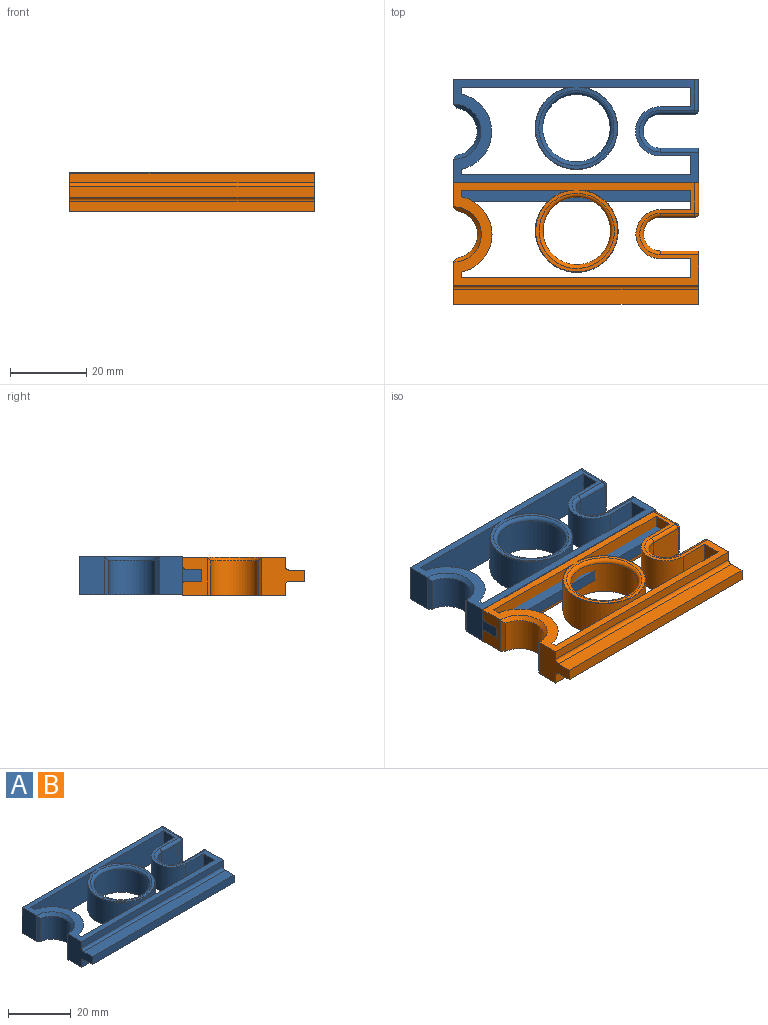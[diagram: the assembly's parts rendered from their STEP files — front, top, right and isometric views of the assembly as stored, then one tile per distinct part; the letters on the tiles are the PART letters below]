
ASSEMBLY  parts=2 mates=1
PART A: 48 faces, bbox 64.2x32x10.1 mm
  f0: plane 64.13x26.92mm, normal (0,0,1), area 447.9mm2, adj f1,f2,f3,f4,f5,f9,f17,f18
  f1: plane 10x8.96mm, normal (1,0,0), area 89.2mm2, adj f0,f5,f7,f13,f14,f17
  f2: plane 11.13x10mm, normal (-1,0,0), area 76.7mm2, adj f0,f5,f7,f21,f22,f36,f38,f39
  f3: plane 64.13x10mm, normal (0,1,0), area 640.9mm2, adj f0,f4,f6,f7,f43,f47
  f4: plane 10x6.46mm, normal (-1,0,0), area 64.6mm2, adj f0,f3,f7,f20,f21
  f5: plane 64.13x10mm, normal (0,-1,0), area 321.3mm2, adj f0,f1,f2,f7,f37,f40,f41
  f6: plane 8.1x8mm, normal (1,0,0), area 64.8mm2, adj f3,f43,f45,f47
  f7: plane 64.13x26.92mm, normal (0,0,-1), area 488.3mm2, adj f1,f2,f3,f4,f5,f8,f10,f14
  f8: cylinder r=8.83mm len=17.67mm, axis (0,0,1), area 499.5mm2, adj f7,f9
  f9: torus R=9.83mm, axis (0,0,1), area 90.8mm2, adj f0,f8
  f10: cylinder r=6.24mm len=12.35mm, axis (0,0,1), area 160.5mm2, adj f7,f20,f21,f22
  f11: plane 9x8mm, normal (0,-1,0), area 72mm2, adj f12,f16,f19,f45
  f12: cylinder r=4.43mm len=8.86mm, axis (0,0,1), area 111.4mm2, adj f11,f13,f15,f18
  f13: plane 10x8mm, normal (0,1,0), area 80mm2, adj f1,f12,f14,f17
  f14: cylinder r=1mm len=10mm, axis (1,0,0), area 15.7mm2, adj f1,f7,f13,f15
  f15: torus R=5.43mm, axis (0,0,1), area 23.7mm2, adj f7,f12,f14,f16
  f16: cylinder r=1mm len=9mm, axis (-1,0,0), area 14.1mm2, adj f7,f11,f15,f46
  f17: cylinder r=1mm len=10mm, axis (-1,0,0), area 15.7mm2, adj f0,f1,f13,f18
  f18: torus R=5.43mm, axis (0,0,1), area 23.7mm2, adj f0,f12,f17,f19
  f19: cylinder r=1mm len=9mm, axis (1,0,0), area 14.1mm2, adj f0,f11,f18,f44
  f20: plane 10.01x1.07mm, normal (-0.76,-0.66,0), area 12.4mm2, adj f4,f7,f10,f21
  f21: cone r=6.24mm half-angle=45deg, axis (0,0,1), area 28.7mm2, adj f0,f2,f4,f10,f20,f22
  f22: plane 10.01x1.07mm, normal (-0.76,0.66,0), area 12.4mm2, adj f2,f7,f10,f21
  f23: plane 29.51x10.09mm, normal (0,-1,0), area 285.5mm2, adj f0,f7,f27,f30,f42
  f24: plane 10x4.96mm, normal (-1,0,0), area 49.6mm2, adj f0,f7,f28,f34
  f25: plane 10.04x3.35mm, normal (1,0,0), area 31.4mm2, adj f0,f7,f28,f31,f35
  f26: plane 29.21x10.09mm, normal (0,-1,0), area 282.5mm2, adj f0,f7,f29,f30,f42
  f27: plane 10.04x3.68mm, normal (1,0,0), area 34.7mm2, adj f0,f7,f23,f31,f35
  f28: plane 60.13x10mm, normal (0,1,0), area 601.3mm2, adj f0,f7,f24,f25
  f29: plane 10x5.1mm, normal (-1,0,0), area 51mm2, adj f0,f7,f26,f32
  f30: cylinder r=10.83mm len=21.67mm, axis (0,0,1), area 640.8mm2, adj f7,f23,f26,f42
  f31: cylinder r=8.24mm len=15.97mm, axis (0,0,1), area 178.1mm2, adj f7,f25,f27,f35
  f32: plane 10x8mm, normal (0,1,0), area 80mm2, adj f0,f7,f29,f33
  f33: cylinder r=6.43mm len=12.86mm, axis (0,0,1), area 202.1mm2, adj f0,f7,f32,f34
  f34: plane 10x8mm, normal (0,-1,0), area 80mm2, adj f0,f7,f24,f33
  f35: cone r=7.65mm half-angle=45deg, axis (0,0,1), area 63.7mm2, adj f0,f25,f27,f31
  f36: plane 64x4mm, normal (0,0,-1), area 256mm2, adj f2,f37,f39,f41
  f37: plane 5x5mm, normal (1,0,0), area 15.4mm2, adj f5,f36,f38,f39,f40,f41
  f38: plane 64x4mm, normal (0,0,1), area 256mm2, adj f2,f37,f39,f40
  f39: plane 64x3mm, normal (0,-1,0), area 192mm2, adj f2,f36,f37,f38
  f40: cylinder r=1mm len=64mm, axis (1,0,0), area 100.5mm2, adj f2,f5,f37,f38
  f41: cylinder r=1mm len=64mm, axis (-1,0,0), area 100.5mm2, adj f2,f5,f36,f37
  f42: torus R=10.73mm, axis (0,0,1), area 10.3mm2, adj f0,f23,f26,f30
  f43: cylinder r=1mm len=8.1mm, axis (0,-1,0), area 12.7mm2, adj f0,f3,f6,f44
  f44: sphere r=1mm, area 1.6mm2, adj f19,f43,f45
  f45: cylinder r=1mm len=8mm, axis (0,0,-1), area 12.6mm2, adj f6,f11,f44,f46
  f46: sphere r=1mm, area 1.6mm2, adj f16,f45,f47
  f47: cylinder r=1mm len=8.1mm, axis (0,1,0), area 12.7mm2, adj f3,f6,f7,f46
PART B: same geometry as A
PLACE A t=(5.66,17.96,16.09)mm
PLACE B t=(5.75,-8.96,15.96)mm
MATE slider B.f3 <-> A.f5  axis (0,1,0) through (5.58,3.75,20.96)mm
